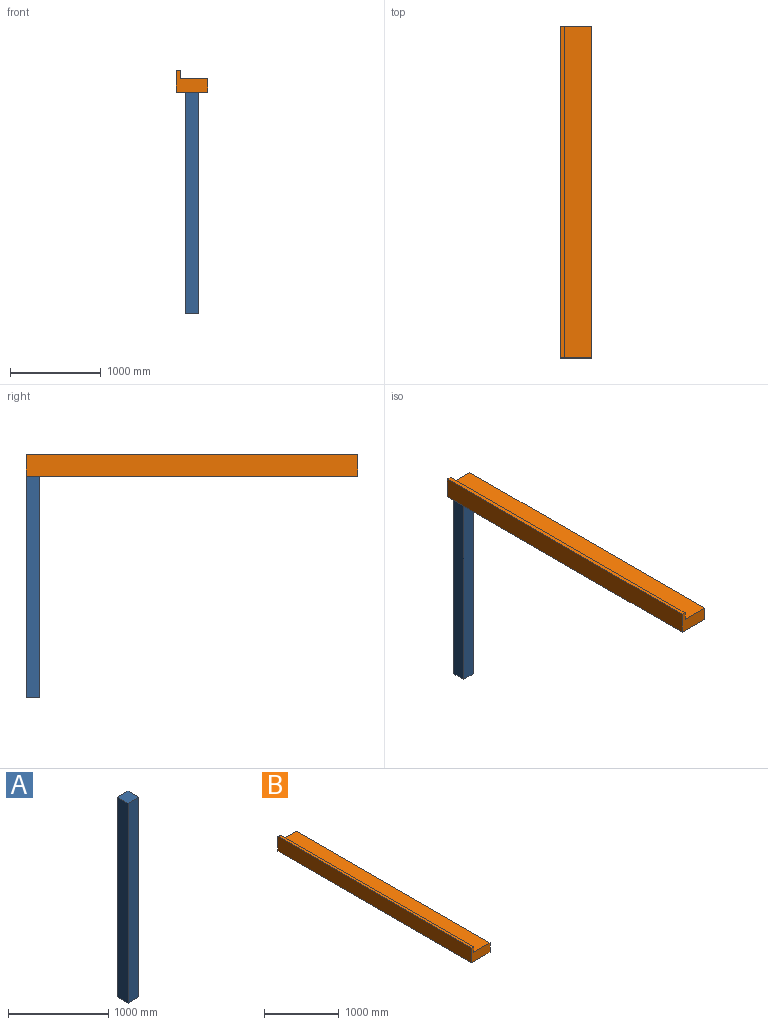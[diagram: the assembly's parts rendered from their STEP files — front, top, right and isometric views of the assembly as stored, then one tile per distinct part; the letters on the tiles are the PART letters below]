
ASSEMBLY  parts=2 mates=1
PART A: 6 faces, bbox 152.4x152.4x2438.4 mm
  f0: plane 2438.4x152.4mm, normal (0,-1,0), area 371612.2mm2, adj f1,f3,f4,f5
  f1: plane 2438.4x152.4mm, normal (1,0,0), area 371612.2mm2, adj f0,f2,f4,f5
  f2: plane 2438.4x152.4mm, normal (0,1,0), area 371612.2mm2, adj f1,f3,f4,f5
  f3: plane 2438.4x152.4mm, normal (-1,0,0), area 371612.2mm2, adj f0,f2,f4,f5
  f4: plane 152.4x152.4mm, normal (0,0,1), area 23225.8mm2, adj f0,f1,f2,f3
  f5: plane 152.4x152.4mm, normal (0,0,-1), area 23225.8mm2, adj f0,f1,f2,f3
PART B: 8 faces, bbox 349.3x3657.6x241.3 mm
  f0: plane 3657.6x304.8mm, normal (0,0,1), area 1114836.5mm2, adj f1,f2,f3,f6
  f1: plane 349.25x241.3mm, normal (0,-1,0), area 57177.3mm2, adj f0,f2,f4,f5,f6,f7
  f2: plane 3657.6x152.4mm, normal (1,0,0), area 557418.2mm2, adj f0,f1,f3,f4
  f3: plane 349.25x241.3mm, normal (0,1,0), area 57177.3mm2, adj f0,f2,f4,f5,f6,f7
  f4: plane 3657.6x349.25mm, normal (0,0,-1), area 1277416.8mm2, adj f1,f2,f3,f5
  f5: plane 3657.6x241.3mm, normal (-1,0,0), area 882578.9mm2, adj f1,f3,f4,f7
  f6: plane 3657.6x88.9mm, normal (1,0,0), area 325160.6mm2, adj f0,f1,f3,f7
  f7: plane 3657.6x44.45mm, normal (0,0,1), area 162580.3mm2, adj f1,f3,f5,f6
PLACE A t=(75.48,-77.38,-1219.2)mm
PLACE B t=(173.9,-3582.58,1219.2)mm
MATE planar B.f4 <-> A.f4  axis (0,0,-1) through (-0.72,75.02,1219.2)mm
